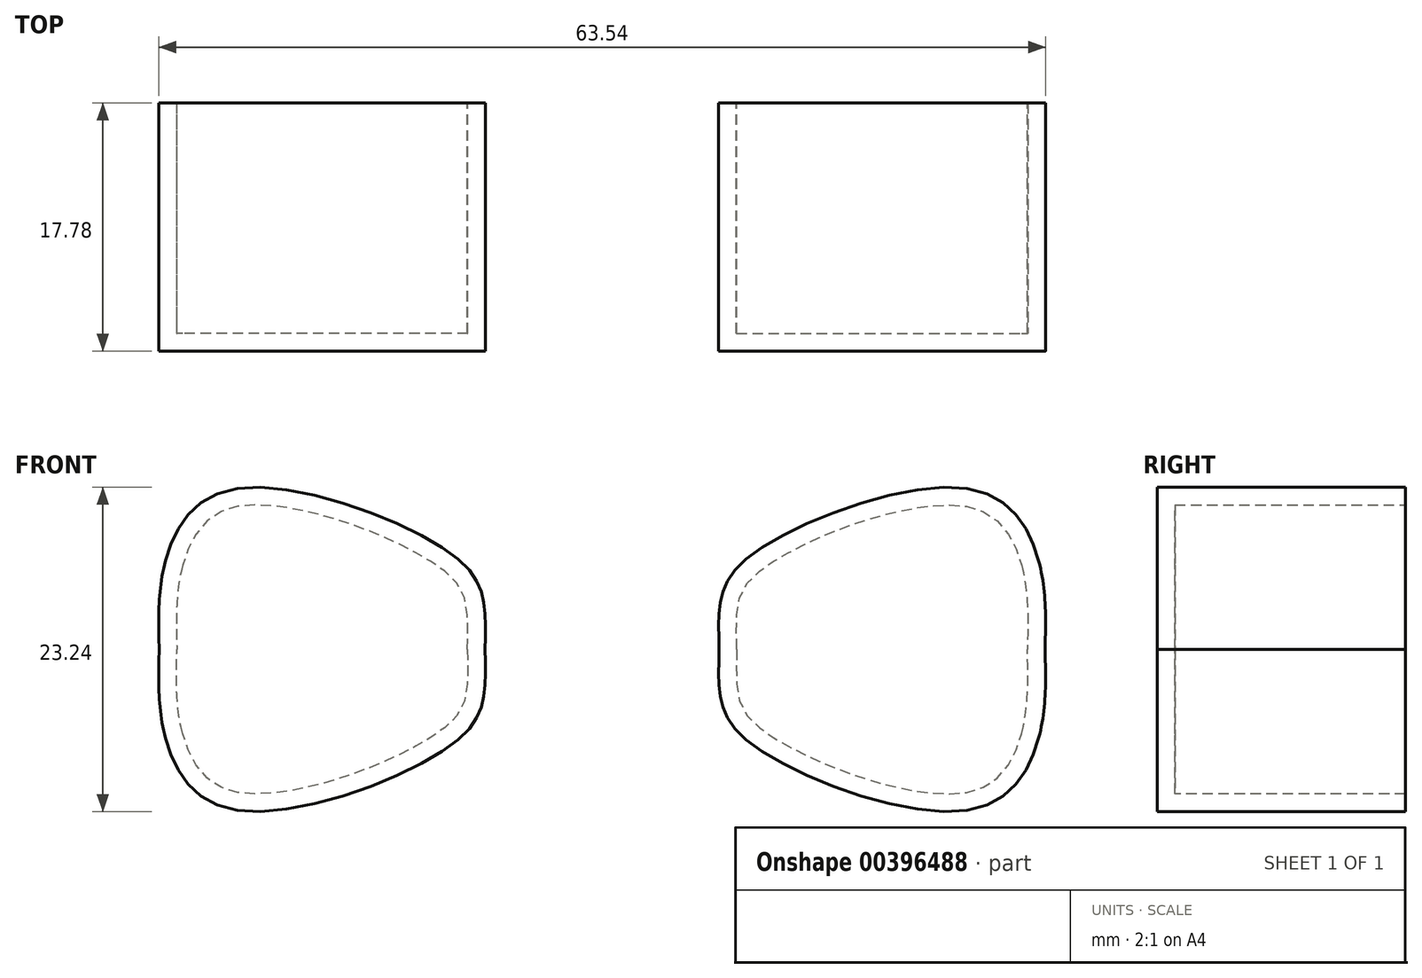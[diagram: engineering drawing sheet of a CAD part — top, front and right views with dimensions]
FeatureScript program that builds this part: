
annotation { "Feature Type Name" : "Feature", "Feature Type Description" : "" }
export const myFeature = defineFeature(function(context is Context, id is Id, definition is map)
    precondition{}
    {
        {
            var Q0;
            Q0=qCreatedBy(makeId("Front.planeOp"),FACE);
            var sketch = newSketch(context, id + "F0", { "sketchPlane" : qUnion([Q0])});
            skLineSegment(sketch, "E0", {"start": v(0, 45.77) * mm, "end": v(0, -51.28) * mm});
            skSolve(sketch);
        }
        {
            var Q0;
            Q0=qCreatedBy(makeId("Front.planeOp"),FACE);
            var sketch = newSketch(context, id + "F1", { "sketchPlane" : qUnion([Q0])});
            skFitSpline(sketch, "E1", {"points": [v(8.38, 0) * mm, v(8.48, 3.34) * mm, v(10.76, 6.8) * mm, v(26.54, 11.46) * mm, v(31.28, 6.35) * mm, v(31.73, 0) * mm], "startDerivative": vector(-0.82, 24.55) * mm, "endDerivative": vector(-0.9, -32.74) * mm});
            skFitSpline(sketch, "E2.MirrorCS", {"points": [v(-8.38, 0) * mm, v(-8.48, 3.34) * mm, v(-10.76, 6.8) * mm, v(-26.54, 11.46) * mm, v(-31.28, 6.35) * mm, v(-31.73, 0) * mm], "startDerivative": vector(0.82, 24.55) * mm, "endDerivative": vector(0.9, -32.74) * mm});
            skFitSpline(sketch, "E3.MirrorCS", {"points": [v(-8.38, 0) * mm, v(-8.48, -3.34) * mm, v(-10.76, -6.8) * mm, v(-26.54, -11.46) * mm, v(-31.28, -6.35) * mm, v(-31.73, 0) * mm], "startDerivative": vector(0.82, -24.55) * mm, "endDerivative": vector(0.9, 32.74) * mm});
            skFitSpline(sketch, "E4.MirrorCS", {"points": [v(8.38, 0) * mm, v(8.48, -3.34) * mm, v(10.76, -6.8) * mm, v(26.54, -11.46) * mm, v(31.28, -6.35) * mm, v(31.73, 0) * mm], "startDerivative": vector(-0.82, -24.55) * mm, "endDerivative": vector(-0.9, 32.74) * mm});
            skPoint(sketch, "E5.1.internal.orphan", {"position": v(-31.8, 4.6) * mm});
            skPoint(sketch, "E5.2.internal.orphan", {"position": v(-32.25, 2.1) * mm});
            skLineSegment(sketch, "E6", {"start": v(-31.28, 6.35) * mm, "end": v(-31.28, -6.35) * mm});
            skLineSegment(sketch, "E7", {"start": v(31.28, 6.35) * mm, "end": v(31.28, -6.35) * mm});
            skSolve(sketch);
        }
        {
            var Q0;
            Q0=makeQuery(id+"F1.imprint","IMPRINT",FACE,{"disambiguationData":[TD([[makeQuery(id+"F1.imprint","IMPRINT",EDGE,{"derivedFrom":sQuery(id+"F1.wireOp",EDGE,"E2.MirrorCS")}),1.0]])]});
            var Q1;
            Q1=makeQuery(id+"F1.imprint","IMPRINT",FACE,{"disambiguationData":[TD([[makeQuery(id+"F1.imprint","IMPRINT",EDGE,{"derivedFrom":sQuery(id+"F1.wireOp",EDGE,"E1")}),-1.0]])]});
            extrude(context, id + "F2", {"entities" : qUnion([Q0, Q1]), "depth" : 17.78 * mm});
        }
        {
            var Q0;
            Q0=makeQuery(id+"F2.opExtrude","CAP_FACE",FACE,{"disambiguationData":[OSD([sQuery(id+"F1.wireOp",EDGE,"E2.MirrorCS"),sQuery(id+"F1.wireOp",EDGE,"E3.MirrorCS"),sQuery(id+"F1.wireOp",EDGE,"E6")])],"isStart":true});
            var Q1;
            Q1=makeQuery(id+"F2.opExtrude","CAP_FACE",FACE,{"disambiguationData":[OSD([sQuery(id+"F1.wireOp",EDGE,"E1"),sQuery(id+"F1.wireOp",EDGE,"E4.MirrorCS"),sQuery(id+"F1.wireOp",EDGE,"E7")])],"isStart":true});
            shell(context, id + "F3", {"entities" : qUnion([Q0, Q1]), "thickness" : 1.27 * mm});
        }
    });
